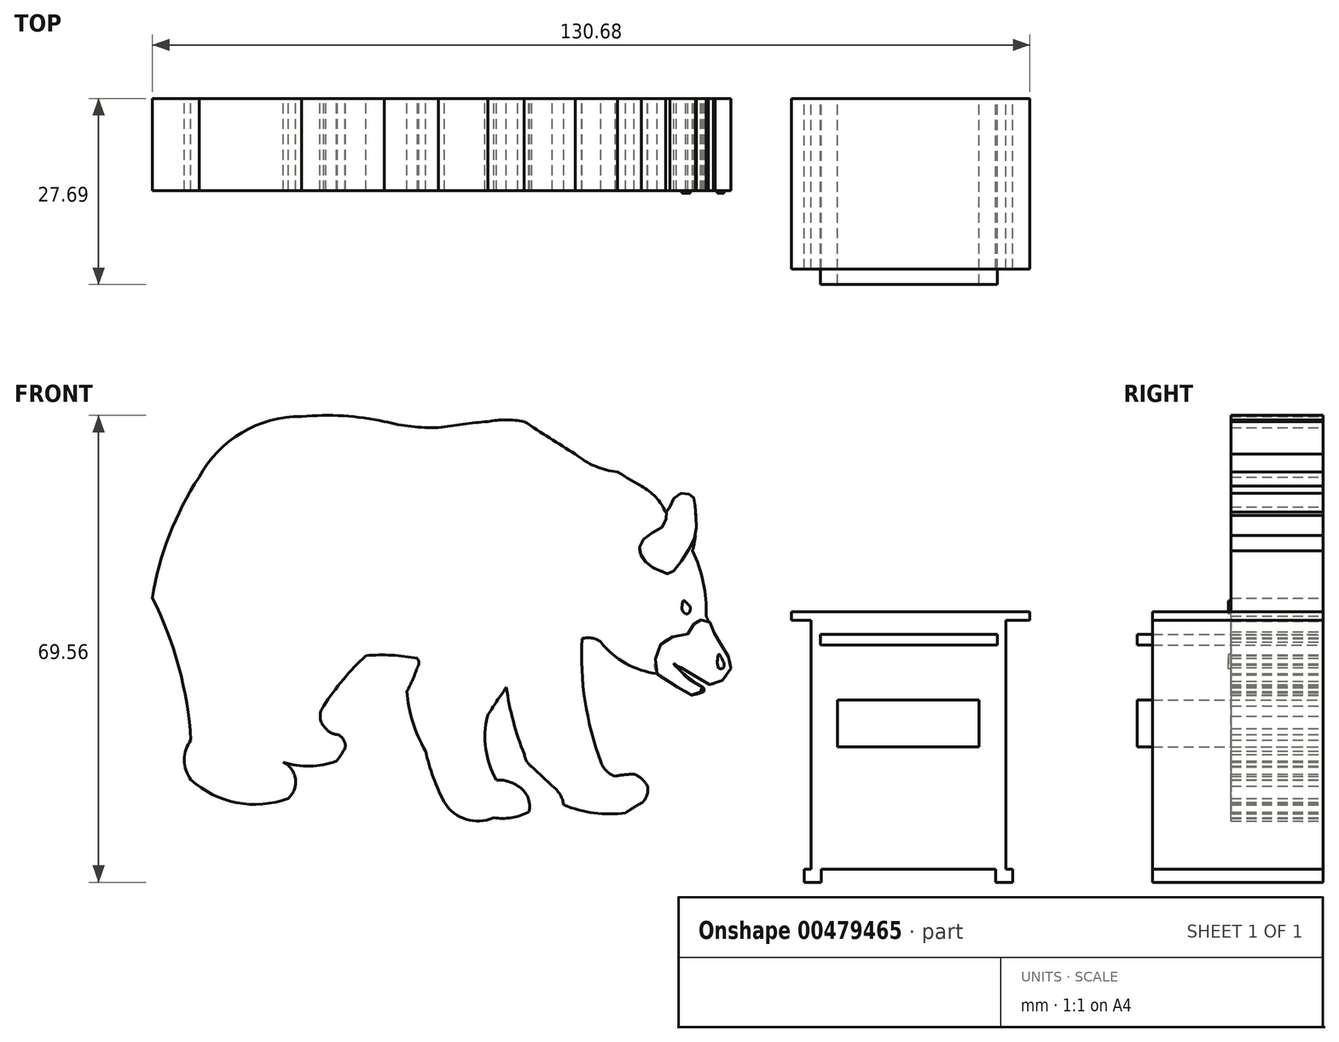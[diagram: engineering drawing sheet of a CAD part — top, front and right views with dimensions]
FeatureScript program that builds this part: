
annotation { "Feature Type Name" : "Feature", "Feature Type Description" : "" }
export const myFeature = defineFeature(function(context is Context, id is Id, definition is map)
    precondition{}
    {
        {
            var Q0;
            Q0=qCreatedBy(makeId("Front.planeOp"),FACE);
            var sketch = newSketch(context, id + "F0", { "sketchPlane" : qUnion([Q0])});
            skArc(sketch, "E0", {"start": v(-31.22, 8.3) * mm, "mid": v(-33.93, 8.55) * mm, "end": v(-36.64, 8.3) * mm});
            skArc(sketch, "E1", {"start": v(-36.64, 8.3) * mm, "mid": v(-40.3, 7.9) * mm, "end": v(-43.96, 7.37) * mm});
            skArc(sketch, "E2", {"start": v(-52.02, 8.3) * mm, "mid": v(-48.02, 7.55) * mm, "end": v(-43.96, 7.37) * mm});
            skArc(sketch, "E3", {"start": v(-52.02, 8.3) * mm, "mid": v(-58.16, 9.13) * mm, "end": v(-64.36, 9.05) * mm});
            skArc(sketch, "E4", {"start": v(-64.36, 9.05) * mm, "mid": v(-73.26, 6.64) * mm, "end": v(-79.64, 0) * mm});
            skArc(sketch, "E5", {"start": v(-79.64, 0) * mm, "mid": v(-84.06, -8.64) * mm, "end": v(-86.58, -18) * mm});
            skArc(sketch, "E6", {"start": v(-80.86, -39.17) * mm, "mid": v(-82.65, -28.3) * mm, "end": v(-86.58, -18) * mm});
            skArc(sketch, "E7", {"start": v(-80.86, -39.17) * mm, "mid": v(-81.83, -42.12) * mm, "end": v(-80.86, -45.06) * mm});
            skArc(sketch, "E8", {"start": v(-80.86, -45.06) * mm, "mid": v(-74, -48.5) * mm, "end": v(-66.36, -47.85) * mm});
            skArc(sketch, "E9", {"start": v(-66.36, -47.85) * mm, "mid": v(-65.33, -44.66) * mm, "end": v(-67.69, -42.27) * mm});
            skArc(sketch, "E10", {"start": v(-67.69, -42.27) * mm, "mid": v(-63.42, -43.06) * mm, "end": v(-59.15, -42.27) * mm});
            skArc(sketch, "E11", {"start": v(-59.15, -42.27) * mm, "mid": v(-58.42, -41.28) * mm, "end": v(-57.87, -40.19) * mm});
            skArc(sketch, "E12", {"start": v(-57.87, -40.19) * mm, "mid": v(-58.12, -39.08) * mm, "end": v(-59, -38.37) * mm});
            skArc(sketch, "E13", {"start": v(-60.77, -37.45) * mm, "mid": v(-59.98, -38.08) * mm, "end": v(-59, -38.37) * mm});
            skArc(sketch, "E14", {"start": v(-61.08, -34.1) * mm, "mid": v(-61.6, -35.84) * mm, "end": v(-60.77, -37.45) * mm});
            skArc(sketch, "E15", {"start": v(-54.79, -26.59) * mm, "mid": v(-58.17, -30.15) * mm, "end": v(-61.08, -34.1) * mm});
            skArc(sketch, "E16", {"start": v(-47.12, -26.99) * mm, "mid": v(-50.94, -26.53) * mm, "end": v(-54.79, -26.59) * mm});
            skArc(sketch, "E17", {"start": v(-47.12, -28.35) * mm, "mid": v(-46.9, -27.67) * mm, "end": v(-47.12, -26.99) * mm});
            skArc(sketch, "E18", {"start": v(-48.69, -31.92) * mm, "mid": v(-47.82, -30.17) * mm, "end": v(-47.12, -28.35) * mm});
            skArc(sketch, "E19", {"start": v(-48.69, -31.92) * mm, "mid": v(-47.8, -36.52) * mm, "end": v(-45.91, -40.8) * mm});
            skArc(sketch, "E20", {"start": v(-45.91, -40.8) * mm, "mid": v(-44.76, -44.73) * mm, "end": v(-43.09, -48.46) * mm});
            skArc(sketch, "E21", {"start": v(-43.09, -48.46) * mm, "mid": v(-39.85, -50.96) * mm, "end": v(-35.76, -50.75) * mm});
            skArc(sketch, "E22", {"start": v(-35.76, -50.75) * mm, "mid": v(-33.07, -50.73) * mm, "end": v(-30.52, -49.9) * mm});
            skArc(sketch, "E23", {"start": v(-30.52, -49.9) * mm, "mid": v(-30.68, -47.68) * mm, "end": v(-32.16, -46.03) * mm});
            skArc(sketch, "E24", {"start": v(-32.16, -46.03) * mm, "mid": v(-33.7, -45.3) * mm, "end": v(-35.38, -45.12) * mm});
            skArc(sketch, "E25", {"start": v(-36.7, -35.6) * mm, "mid": v(-36.94, -40.48) * mm, "end": v(-35.38, -45.12) * mm});
            skArc(sketch, "E26", {"start": v(-33.86, -31.32) * mm, "mid": v(-35.33, -33.43) * mm, "end": v(-36.7, -35.6) * mm});
            skArc(sketch, "E27", {"start": v(-33.86, -31.32) * mm, "mid": v(-32.83, -36.39) * mm, "end": v(-31.2, -41.3) * mm});
            skArc(sketch, "E28", {"start": v(-31.2, -41.3) * mm, "mid": v(-30.82, -42.33) * mm, "end": v(-30.1, -43.14) * mm});
            skArc(sketch, "E29", {"start": v(-27.03, -46) * mm, "mid": v(-28.56, -44.57) * mm, "end": v(-30.1, -43.14) * mm});
            skArc(sketch, "E30", {"start": v(-25.34, -48.81) * mm, "mid": v(-25.89, -47.23) * mm, "end": v(-27.03, -46) * mm});
            skArc(sketch, "E31", {"start": v(-25.34, -48.81) * mm, "mid": v(-20.8, -50.03) * mm, "end": v(-16.1, -50) * mm});
            skArc(sketch, "E32", {"start": v(-13.66, -48.5) * mm, "mid": v(-14.9, -49.22) * mm, "end": v(-16.1, -50) * mm});
            skArc(sketch, "E33", {"start": v(-13.66, -48.5) * mm, "mid": v(-12.92, -47.36) * mm, "end": v(-12.87, -46) * mm});
            skArc(sketch, "E34", {"start": v(-12.87, -46) * mm, "mid": v(-13.7, -44.95) * mm, "end": v(-14.85, -44.26) * mm});
            skArc(sketch, "E35", {"start": v(-14.85, -44.26) * mm, "mid": v(-16.26, -44.34) * mm, "end": v(-17.65, -44.55) * mm});
            skArc(sketch, "E36", {"start": v(-19.77, -42.43) * mm, "mid": v(-18.98, -43.76) * mm, "end": v(-17.65, -44.55) * mm});
            skArc(sketch, "E37", {"start": v(-22.57, -24.06) * mm, "mid": v(-22.14, -33.4) * mm, "end": v(-19.77, -42.43) * mm});
            skArc(sketch, "E38", {"start": v(-19.77, -24.56) * mm, "mid": v(-21.11, -23.97) * mm, "end": v(-22.57, -24.06) * mm});
            skArc(sketch, "E39", {"start": v(-19.77, -24.56) * mm, "mid": v(-16.03, -27.78) * mm, "end": v(-11.33, -29.27) * mm});
            skArc(sketch, "E40", {"start": v(-11.33, -29.27) * mm, "mid": v(-8.82, -30.87) * mm, "end": v(-6.3, -32.46) * mm});
            skArc(sketch, "E41", {"start": v(-6.3, -32.46) * mm, "mid": v(-2.94, -31.13) * mm, "end": v(-0.48, -28.49) * mm});
            skArc(sketch, "E42", {"start": v(-0.48, -28.49) * mm, "mid": v(-0.62, -27.26) * mm, "end": v(-1.2, -26.17) * mm});
            skArc(sketch, "E43", {"start": v(-4.1, -20.69) * mm, "mid": v(-2.78, -23.5) * mm, "end": v(-1.2, -26.17) * mm});
            skArc(sketch, "E44", {"start": v(-4.1, -20.69) * mm, "mid": v(-4.52, -15.71) * mm, "end": v(-6.15, -11) * mm});
            skArc(sketch, "E45", {"start": v(-6.15, -11) * mm, "mid": v(-5.6, -6.95) * mm, "end": v(-6.15, -2.9) * mm});
            skArc(sketch, "E46", {"start": v(-6.15, -2.9) * mm, "mid": v(-7.31, -2.57) * mm, "end": v(-8.48, -2.9) * mm});
            skArc(sketch, "E47", {"start": v(-10.12, -5.24) * mm, "mid": v(-9.26, -4.1) * mm, "end": v(-8.48, -2.9) * mm});
            skArc(sketch, "E48", {"start": v(-10.12, -5.24) * mm, "mid": v(-11.62, -2.99) * mm, "end": v(-13.76, -1.34) * mm});
            skArc(sketch, "E49", {"start": v(-31.22, 8.3) * mm, "mid": v(-27.43, 5.84) * mm, "end": v(-23.6, 3.45) * mm});
            skArc(sketch, "E50", {"start": v(-23.6, 3.45) * mm, "mid": v(-20.65, 1.64) * mm, "end": v(-17.29, 0.8) * mm});
            skArc(sketch, "E51", {"start": v(-17.29, 0.8) * mm, "mid": v(-15.54, -0.3) * mm, "end": v(-13.76, -1.34) * mm});
            skArc(sketch, "E52", {"start": v(-7.54, -24.4) * mm, "mid": v(-5.54, -22.8) * mm, "end": v(-4.1, -20.69) * mm});
            skArc(sketch, "E53", {"start": v(-7.54, -24.4) * mm, "mid": v(-10.46, -26.03) * mm, "end": v(-11.33, -29.27) * mm});
            skSolve(sketch);
        }
        {
            var Q0;
            Q0 = qSketchRegion(id + "F0", true);
            extrude(context, id + "F1", {"entities" : qUnion([Q0]), "depth" : 13.72 * mm});
        }
        {
            var Q0;
            Q0=qCreatedBy(makeId("Front.planeOp"),FACE);
            var sketch = newSketch(context, id + "F2", { "sketchPlane" : qUnion([Q0])});
            skArc(sketch, "E54", {"start": v(-4.03, -30.74) * mm, "mid": v(-6.46, -29.19) * mm, "end": v(-8.96, -27.75) * mm});
            skArc(sketch, "E55", {"start": v(-4.03, -30.74) * mm, "mid": v(-3, -30.87) * mm, "end": v(-2.08, -30.36) * mm});
            skArc(sketch, "E56", {"start": v(-8.96, -27.75) * mm, "mid": v(-6.89, -29.76) * mm, "end": v(-4.48, -31.36) * mm});
            skArc(sketch, "E57", {"start": v(-4.48, -31.98) * mm, "mid": v(-4.43, -31.67) * mm, "end": v(-4.48, -31.36) * mm});
            skArc(sketch, "E58", {"start": v(-2.08, -30.36) * mm, "mid": v(-2, -30.34) * mm, "end": v(-1.93, -30.3) * mm});
            skArc(sketch, "E59", {"start": v(-4.48, -31.98) * mm, "mid": v(-2.83, -31.72) * mm, "end": v(-1.93, -30.3) * mm});
            skSolve(sketch);
        }
        {
            var Q0;
            Q0 = qSketchRegion(id + "F2", true);
            extrude(context, id + "F3", {"entities" : qUnion([Q0]), "operationType" : NewBodyOperationType.REMOVE, "depth" : 54.1 * mm});
        }
        {
            var Q0;
            Q0=qCreatedBy(makeId("Front.planeOp"),FACE);
            var sketch = newSketch(context, id + "F4", { "sketchPlane" : qUnion([Q0])});
            skFitSpline(sketch, "E60", {"points": [v(-7.17, -20.34) * mm, v(-6.84, -20.36) * mm, v(-6.53, -19.94) * mm, v(-6.53, -19.3) * mm, v(-7.17, -18.56) * mm, v(-7.5, -18.39) * mm, v(-7.66, -18.95) * mm, v(-7.66, -19.76) * mm, v(-7.17, -20.34) * mm]});
            skFitSpline(sketch, "E61", {"points": [v(-2.25, -28.43) * mm, v(-2.44, -27.54) * mm, v(-2.35, -26.65) * mm, v(-2.19, -26.38) * mm, v(-1.81, -26.94) * mm, v(-1.52, -27.54) * mm, v(-1.48, -28.31) * mm, v(-1.88, -28.54) * mm, v(-2.25, -28.43) * mm]});
            skSolve(sketch);
        }
        {
            var Q0;
            Q0 = qSketchRegion(id + "F4", true);
            extrude(context, id + "F5", {"entities" : qUnion([Q0]), "operationType" : NewBodyOperationType.ADD, "depth" : 14.1 * mm});
        }
        {
            var Q0;
            Q0=qCreatedBy(makeId("Front.planeOp"),FACE);
            var sketch = newSketch(context, id + "F6", { "sketchPlane" : qUnion([Q0])});
            skPoint(sketch, "E62.3.internal.orphan", {"position": v(0, -28.57) * mm});
            skFitSpline(sketch, "E63", {"points": [v(-11.4, -29.3) * mm, v(-11.67, -27.14) * mm, v(-10.97, -25.03) * mm, v(-9.38, -23.83) * mm, v(-6.9, -23.37) * mm, v(-6.04, -22.24) * mm, v(-5.85, -21.62) * mm, v(-5.06, -21.29) * mm, v(-3.7, -21.45) * mm, v(-3.53, -21.66) * mm, v(-3.12, -22.82) * mm, v(-2.41, -24.1) * mm, v(-1.3, -25.89) * mm, v(-0.55, -27.34) * mm, v(-0.55, -28.83) * mm, v(-2.04, -30.49) * mm, v(-3.61, -30.9) * mm, v(-4.94, -30.11) * mm, v(-8.13, -28.25) * mm, v(-8.92, -27.8) * mm, v(-8.59, -28.3) * mm, v(-7.92, -28.87) * mm, v(-6.93, -29.9) * mm, v(-5.02, -31.07) * mm, v(-4.57, -31.36) * mm, v(-4.48, -31.81) * mm, v(-5.52, -32.19) * mm, v(-6.27, -32.48) * mm, v(-6.93, -32.06) * mm, v(-11.4, -29.3) * mm]});
            skFitSpline(sketch, "E64", {"points": [v(-13.99, -10.39) * mm, v(-12.8, -8.68) * mm, v(-10.3, -7.04) * mm, v(-10.05, -5.23) * mm, v(-9.6, -4.6) * mm, v(-8.52, -2.69) * mm, v(-6.77, -2.48) * mm, v(-5.97, -3.03) * mm, v(-5.73, -4.95) * mm, v(-5.62, -8.3) * mm, v(-7.3, -11.71) * mm, v(-9.53, -14.36) * mm, v(-10.33, -14.19) * mm, v(-11.97, -13.49) * mm, v(-13.64, -11.96) * mm, v(-13.99, -10.39) * mm]});
            skSolve(sketch);
        }
        {
            var Q0;
            Q0 = qSketchRegion(id + "F6", true);
            extrude(context, id + "F7", {"entities" : qUnion([Q0]), "operationType" : NewBodyOperationType.ADD, "depth" : 13.74 * mm});
        }
        {
            var Q0;
            Q0=qCreatedBy(makeId("Front.planeOp"),FACE);
            var sketch = newSketch(context, id + "F8", { "sketchPlane" : qUnion([Q0])});
            skLineSegment(sketch, "E65.bottom", {"start": v(11.5, -21.35) * mm, "end": v(40.5, -21.35) * mm});
            skLineSegment(sketch, "E65.top", {"start": v(11.5, -58.42) * mm, "end": v(40.5, -58.42) * mm});
            skLineSegment(sketch, "E65.left", {"start": v(11.5, -21.35) * mm, "end": v(11.5, -58.42) * mm});
            skLineSegment(sketch, "E65.right", {"start": v(40.5, -21.35) * mm, "end": v(40.5, -58.42) * mm});
            skLineSegment(sketch, "E66", {"start": v(8.6, -21.35) * mm, "end": v(44.1, -21.35) * mm});
            skLineSegment(sketch, "E67", {"start": v(44.1, -21.35) * mm, "end": v(44.1, -20.02) * mm});
            skLineSegment(sketch, "E68", {"start": v(44.1, -20.02) * mm, "end": v(8.6, -20.02) * mm});
            skLineSegment(sketch, "E69", {"start": v(8.6, -20.02) * mm, "end": v(8.6, -21.35) * mm});
            skLineSegment(sketch, "E70", {"start": v(11.5, -58.42) * mm, "end": v(10.48, -58.42) * mm});
            skLineSegment(sketch, "E71", {"start": v(10.48, -58.42) * mm, "end": v(10.48, -60.35) * mm});
            skLineSegment(sketch, "E72", {"start": v(10.48, -60.35) * mm, "end": v(13.02, -60.35) * mm});
            skLineSegment(sketch, "E73", {"start": v(13.02, -60.35) * mm, "end": v(13.02, -58.42) * mm});
            skLineSegment(sketch, "E74", {"start": v(13.02, -58.42) * mm, "end": v(10.48, -58.42) * mm});
            skLineSegment(sketch, "E75", {"start": v(40.5, -58.42) * mm, "end": v(41.53, -58.42) * mm});
            skLineSegment(sketch, "E76", {"start": v(41.53, -58.42) * mm, "end": v(41.53, -60.35) * mm});
            skLineSegment(sketch, "E77", {"start": v(41.53, -60.35) * mm, "end": v(38.99, -60.35) * mm});
            skLineSegment(sketch, "E78", {"start": v(38.99, -60.35) * mm, "end": v(38.99, -58.42) * mm});
            skSolve(sketch);
        }
        {
            var Q0;
            Q0 = qSketchRegion(id + "F8", true);
            extrude(context, id + "F9", {"entities" : qUnion([Q0]), "depth" : 25.4 * mm});
        }
        {
            var Q0;
            Q0=qCreatedBy(makeId("Front.planeOp"),FACE);
            var sketch = newSketch(context, id + "F10", { "sketchPlane" : qUnion([Q0])});
            skLineSegment(sketch, "E79", {"start": v(12.88, -23.44) * mm, "end": v(39.25, -23.44) * mm});
            skLineSegment(sketch, "E80", {"start": v(39.25, -23.44) * mm, "end": v(39.25, -25) * mm});
            skLineSegment(sketch, "E81", {"start": v(39.25, -25) * mm, "end": v(12.88, -25) * mm});
            skLineSegment(sketch, "E82", {"start": v(12.88, -25) * mm, "end": v(12.88, -23.44) * mm});
            skLineSegment(sketch, "E83", {"start": v(15.47, -33.22) * mm, "end": v(15.47, -40.18) * mm});
            skLineSegment(sketch, "E84", {"start": v(15.47, -40.18) * mm, "end": v(36.51, -40.18) * mm});
            skLineSegment(sketch, "E85", {"start": v(36.51, -40.18) * mm, "end": v(36.51, -33.22) * mm});
            skLineSegment(sketch, "E86", {"start": v(36.51, -33.22) * mm, "end": v(15.47, -33.22) * mm});
            skSolve(sketch);
        }
        {
            var Q0;
            Q0 = qSketchRegion(id + "F10", true);
            extrude(context, id + "F11", {"entities" : qUnion([Q0]), "depth" : 27.7 * mm});
        }
    });
